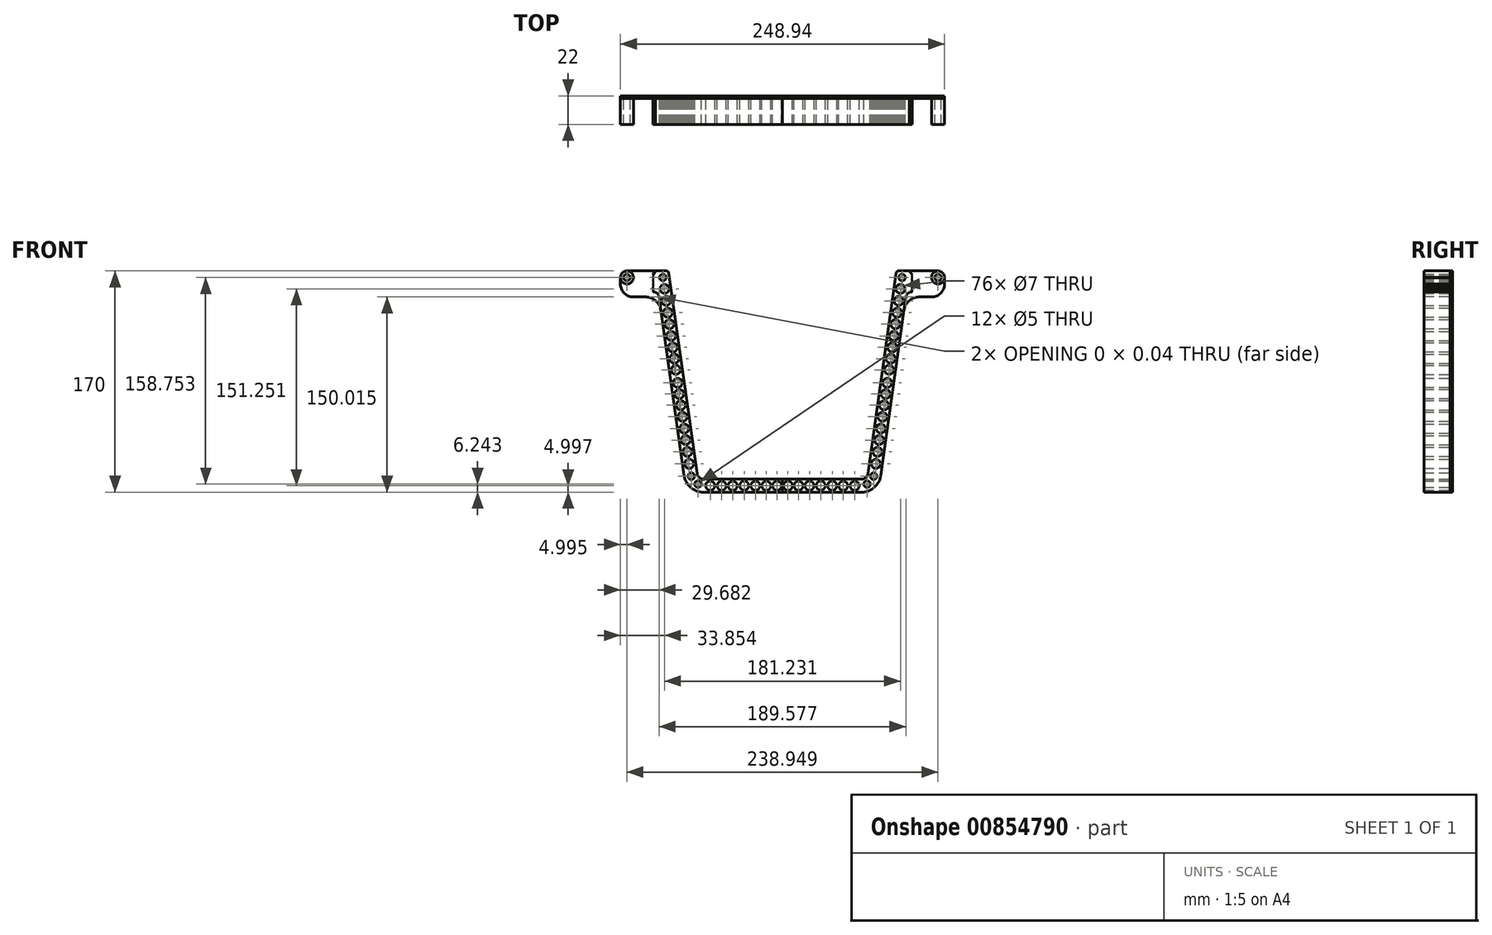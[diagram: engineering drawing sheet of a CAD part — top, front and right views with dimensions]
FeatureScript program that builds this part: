
annotation { "Feature Type Name" : "Feature", "Feature Type Description" : "" }
export const myFeature = defineFeature(function(context is Context, id is Id, definition is map)
    precondition{}
    {
        {
            var Q0;
            Q0=qCreatedBy(makeId("Front.planeOp"),FACE);
            var sketch = newSketch(context, id + "F0", { "sketchPlane" : qUnion([Q0])});
            skLineSegment(sketch, "E0", {"start": v(0, 81.83) * mm, "end": v(0, -78.17) * mm, "construction": true});
            skLineSegment(sketch, "E1", {"start": v(0, -78.17) * mm, "end": v(-65, -78.17) * mm, "construction": true});
            skLineSegment(sketch, "E2", {"start": v(0, 81.83) * mm, "end": v(-87.5, 81.83) * mm, "construction": true});
            skLineSegment(sketch, "E3", {"start": v(-87.5, 81.83) * mm, "end": v(-65, -78.17) * mm, "construction": true});
            skLineSegment(sketch, "E4", {"start": v(-92.55, 81.83) * mm, "end": v(-69.88, -79.36) * mm, "construction": true});
            skLineSegment(sketch, "E5", {"start": v(-87.26, 80.1) * mm, "end": v(-65.6, -73.87) * mm});
            skLineSegment(sketch, "E6", {"start": v(0, -78.17) * mm, "end": v(-60.65, -78.17) * mm});
            skPoint(sketch, "E7.visualSharp", {"position": v(-65, -78.17) * mm});
            skArc(sketch, "E7.filletArc", {"start": v(-65.6, -73.87) * mm, "mid": v(-63.93, -76.95) * mm, "end": v(-60.65, -78.17) * mm});
            skLineSegment(sketch, "E8.0", {"start": v(0, -88.17) * mm, "end": v(-60.65, -88.17) * mm});
            skArc(sketch, "E8.1", {"start": v(-75.5, -75.26) * mm, "mid": v(-70.5, -84.5) * mm, "end": v(-60.65, -88.17) * mm});
            skLineSegment(sketch, "E8.2", {"start": v(-97.4, 80.43) * mm, "end": v(-75.5, -75.26) * mm});
            skLineSegment(sketch, "E9", {"start": v(-89.24, 81.83) * mm, "end": v(-119.47, 81.83) * mm});
            skLineSegment(sketch, "E10", {"start": v(-97.4, 80.43) * mm, "end": v(-97.4, 81.83) * mm});
            skLineSegment(sketch, "E11", {"start": v(-97.4, 81.83) * mm, "end": v(-99.47, 78.83) * mm});
            skLineSegment(sketch, "E12", {"start": v(-119.47, 83.65) * mm, "end": v(-119.47, 55.14) * mm, "construction": true});
            skLineSegment(sketch, "E13", {"start": v(-114.47, 61.83) * mm, "end": v(-94.79, 61.83) * mm});
            skCircle(sketch, "E14", {"center": v(-119.47, 76.83) * mm, "radius": 5 * mm});
            skLineSegment(sketch, "E15", {"start": v(-124.47, 76.98) * mm, "end": v(-124.47, 71.83) * mm});
            skPoint(sketch, "E16.visualSharp", {"position": v(-124.47, 61.83) * mm});
            skArc(sketch, "E16.filletArc", {"start": v(-124.47, 71.83) * mm, "mid": v(-121.54, 64.76) * mm, "end": v(-114.47, 61.83) * mm});
            skCircle(sketch, "E17", {"center": v(-119.47, 76.83) * mm, "radius": 2.5 * mm});
            skArc(sketch, "E18", {"start": v(-93.38, 51.8) * mm, "mid": v(-97.16, 58.9) * mm, "end": v(-104.63, 61.83) * mm});
            skPoint(sketch, "E19.visualSharp", {"position": v(-87.5, 81.83) * mm});
            skArc(sketch, "E19.filletArc", {"start": v(-87.26, 80.1) * mm, "mid": v(-87.93, 81.34) * mm, "end": v(-89.24, 81.83) * mm});
            skLineSegment(sketch, "E20", {"start": v(-119.47, 76.83) * mm, "end": v(-91.85, 76.83) * mm, "construction": true});
            skCircle(sketch, "E21", {"center": v(-91.85, 76.83) * mm, "radius": 2.5 * mm});
            skLineSegment(sketch, "E22.MirrorCS", {"start": v(0, 81.83) * mm, "end": v(87.5, 81.83) * mm, "construction": true});
            skCircle(sketch, "E23", {"center": v(-90.62, 68.08) * mm, "radius": 3.5 * mm});
            skCircle(sketch, "E24", {"center": v(-89.32, 58.86) * mm, "radius": 3.5 * mm});
            skCircle(sketch, "E25", {"center": v(-86.8, 40.96) * mm, "radius": 3.5 * mm});
            skCircle(sketch, "E26", {"center": v(-88.04, 49.78) * mm, "radius": 3.5 * mm});
            skCircle(sketch, "E27", {"center": v(-85.53, 31.92) * mm, "radius": 3.5 * mm});
            skCircle(sketch, "E28", {"center": v(-84.29, 23.08) * mm, "radius": 3.5 * mm});
            skCircle(sketch, "E29", {"center": v(-83.07, 14.45) * mm, "radius": 3.5 * mm});
            skCircle(sketch, "E30", {"center": v(-81.87, 5.86) * mm, "radius": 3.5 * mm});
            skLineSegment(sketch, "E31", {"start": v(-86.11, 0.16) * mm, "end": v(-76.21, 1.55) * mm, "construction": true});
            skCircle(sketch, "E32.MirrorC", {"center": v(-80.46, -4.16) * mm, "radius": 3.5 * mm});
            skCircle(sketch, "E33.MirrorC", {"center": v(-79.25, -12.75) * mm, "radius": 3.5 * mm});
            skCircle(sketch, "E34.MirrorC", {"center": v(-78.04, -21.38) * mm, "radius": 3.5 * mm});
            skCircle(sketch, "E35.MirrorC", {"center": v(-76.8, -30.21) * mm, "radius": 3.5 * mm});
            skCircle(sketch, "E36.MirrorC", {"center": v(-75.52, -39.25) * mm, "radius": 3.5 * mm});
            skCircle(sketch, "E37.MirrorC", {"center": v(-74.28, -48.07) * mm, "radius": 3.5 * mm});
            skCircle(sketch, "E38.MirrorC", {"center": v(-73, -57.15) * mm, "radius": 3.5 * mm});
            skCircle(sketch, "E39.MirrorC", {"center": v(-71.7, -66.37) * mm, "radius": 3.5 * mm});
            skLineSegment(sketch, "E40", {"start": v(0, -83.17) * mm, "end": v(-64.61, -83.17) * mm, "construction": true});
            skCircle(sketch, "E41.MirrorC", {"center": v(-4.17, -83.17) * mm, "radius": 3.5 * mm});
            skCircle(sketch, "E42.MirrorC", {"center": v(-12.38, -83.17) * mm, "radius": 3.5 * mm});
            skCircle(sketch, "E43.MirrorC", {"center": v(-20.76, -83.17) * mm, "radius": 3.5 * mm});
            skCircle(sketch, "E44.MirrorC", {"center": v(-29.37, -83.1) * mm, "radius": 3.5 * mm});
            skCircle(sketch, "E45.MirrorC", {"center": v(-38.19, -83.17) * mm, "radius": 3.5 * mm});
            skCircle(sketch, "E46.MirrorC", {"center": v(-46.66, -83.17) * mm, "radius": 3.5 * mm});
            skCircle(sketch, "E47.MirrorC", {"center": v(-55.45, -83.17) * mm, "radius": 3.5 * mm});
            skCircle(sketch, "E48", {"center": v(-64.89, -81.93) * mm, "radius": 2.5 * mm});
            skCircle(sketch, "E49", {"center": v(-70, -75.84) * mm, "radius": 2.5 * mm});
            skArc(sketch, "E50", {"start": v(-94.79, 61.83) * mm, "mid": v(-96.37, 64.7) * mm, "end": v(-99.47, 65.74) * mm});
            skLineSegment(sketch, "E51", {"start": v(-99.47, 78.83) * mm, "end": v(-99.3, 78.7) * mm});
            skLineSegment(sketch, "E52", {"start": v(-99.3, 78.7) * mm, "end": v(-99.47, 78.58) * mm});
            skLineSegment(sketch, "E53", {"start": v(-99.47, 78.58) * mm, "end": v(-99.3, 78.46) * mm});
            skLineSegment(sketch, "E54", {"start": v(-99.3, 78.46) * mm, "end": v(-99.47, 78.34) * mm});
            skLineSegment(sketch, "E55", {"start": v(-99.47, 78.34) * mm, "end": v(-99.3, 78.21) * mm});
            skLineSegment(sketch, "E56", {"start": v(-99.3, 78.21) * mm, "end": v(-99.47, 78.1) * mm});
            skLineSegment(sketch, "E57", {"start": v(-99.47, 78.1) * mm, "end": v(-99.3, 77.97) * mm});
            skLineSegment(sketch, "E58", {"start": v(-99.3, 77.97) * mm, "end": v(-99.47, 77.84) * mm});
            skLineSegment(sketch, "E59", {"start": v(-99.47, 77.84) * mm, "end": v(-99.3, 77.72) * mm});
            skLineSegment(sketch, "E60", {"start": v(-99.3, 77.72) * mm, "end": v(-99.47, 77.6) * mm});
            skLineSegment(sketch, "E61", {"start": v(-99.47, 77.6) * mm, "end": v(-99.3, 77.48) * mm});
            skLineSegment(sketch, "E62", {"start": v(-99.3, 77.48) * mm, "end": v(-99.47, 77.35) * mm});
            skLineSegment(sketch, "E63", {"start": v(-99.47, 77.35) * mm, "end": v(-99.3, 77.23) * mm});
            skLineSegment(sketch, "E64", {"start": v(-99.3, 77.23) * mm, "end": v(-99.47, 77.1) * mm});
            skLineSegment(sketch, "E65", {"start": v(-99.47, 77.1) * mm, "end": v(-99.3, 76.98) * mm});
            skLineSegment(sketch, "E66", {"start": v(-99.3, 76.98) * mm, "end": v(-99.47, 76.86) * mm});
            skLineSegment(sketch, "E67.MirrorCS", {"start": v(-99.3, 76.67) * mm, "end": v(-99.47, 76.8) * mm});
            skLineSegment(sketch, "E68.MirrorCS", {"start": v(-99.47, 76.55) * mm, "end": v(-99.3, 76.67) * mm});
            skLineSegment(sketch, "E69.MirrorCS", {"start": v(-99.3, 76.42) * mm, "end": v(-99.47, 76.55) * mm});
            skLineSegment(sketch, "E70.MirrorCS", {"start": v(-99.3, 76.18) * mm, "end": v(-99.47, 76.3) * mm});
            skLineSegment(sketch, "E71.MirrorCS", {"start": v(-99.47, 76.06) * mm, "end": v(-99.3, 76.18) * mm});
            skLineSegment(sketch, "E72.MirrorCS", {"start": v(-99.3, 75.93) * mm, "end": v(-99.47, 76.06) * mm});
            skLineSegment(sketch, "E73.MirrorCS", {"start": v(-99.47, 75.8) * mm, "end": v(-99.3, 75.93) * mm});
            skLineSegment(sketch, "E74.MirrorCS", {"start": v(-99.3, 75.69) * mm, "end": v(-99.47, 75.8) * mm});
            skLineSegment(sketch, "E75.MirrorCS", {"start": v(-99.47, 75.56) * mm, "end": v(-99.3, 75.69) * mm});
            skLineSegment(sketch, "E76.MirrorCS", {"start": v(-99.3, 75.44) * mm, "end": v(-99.47, 75.56) * mm});
            skLineSegment(sketch, "E77.MirrorCS", {"start": v(-99.47, 75.32) * mm, "end": v(-99.3, 75.44) * mm});
            skLineSegment(sketch, "E78.MirrorCS", {"start": v(-99.3, 75.2) * mm, "end": v(-99.47, 75.32) * mm});
            skLineSegment(sketch, "E79.MirrorCS", {"start": v(-99.47, 75.07) * mm, "end": v(-99.3, 75.2) * mm});
            skLineSegment(sketch, "E80.MirrorCS", {"start": v(-99.3, 74.95) * mm, "end": v(-99.47, 75.07) * mm});
            skLineSegment(sketch, "E81.MirrorCS", {"start": v(-99.47, 74.83) * mm, "end": v(-99.3, 74.95) * mm});
            skLineSegment(sketch, "E82.MirrorCS", {"start": v(-99.47, 76.3) * mm, "end": v(-99.3, 76.42) * mm});
            skLineSegment(sketch, "E83", {"start": v(-99.47, 74.83) * mm, "end": v(-99.3, 74.7) * mm});
            skLineSegment(sketch, "E84", {"start": v(-99.3, 74.7) * mm, "end": v(-99.47, 74.58) * mm});
            skLineSegment(sketch, "E85", {"start": v(-99.47, 74.58) * mm, "end": v(-99.3, 74.46) * mm});
            skLineSegment(sketch, "E86", {"start": v(-99.3, 74.46) * mm, "end": v(-99.47, 74.33) * mm});
            skLineSegment(sketch, "E87", {"start": v(-99.47, 74.33) * mm, "end": v(-99.3, 74.2) * mm});
            skLineSegment(sketch, "E88", {"start": v(-99.3, 74.2) * mm, "end": v(-99.47, 74.09) * mm});
            skLineSegment(sketch, "E89", {"start": v(-99.47, 74.09) * mm, "end": v(-99.3, 73.96) * mm});
            skLineSegment(sketch, "E90", {"start": v(-99.3, 73.96) * mm, "end": v(-99.47, 73.84) * mm});
            skLineSegment(sketch, "E91", {"start": v(-99.47, 73.84) * mm, "end": v(-99.3, 73.72) * mm});
            skLineSegment(sketch, "E92", {"start": v(-99.3, 73.72) * mm, "end": v(-99.47, 73.6) * mm});
            skLineSegment(sketch, "E93", {"start": v(-99.47, 73.6) * mm, "end": v(-99.3, 73.47) * mm});
            skLineSegment(sketch, "E94", {"start": v(-99.3, 73.47) * mm, "end": v(-99.47, 73.35) * mm});
            skLineSegment(sketch, "E95", {"start": v(-99.47, 73.35) * mm, "end": v(-99.3, 73.23) * mm});
            skLineSegment(sketch, "E96", {"start": v(-99.3, 73.23) * mm, "end": v(-99.47, 73.1) * mm});
            skLineSegment(sketch, "E97", {"start": v(-99.47, 73.1) * mm, "end": v(-99.3, 72.98) * mm});
            skLineSegment(sketch, "E98", {"start": v(-99.3, 72.98) * mm, "end": v(-99.47, 72.86) * mm});
            skLineSegment(sketch, "E99.MirrorCS", {"start": v(-99.3, 72.67) * mm, "end": v(-99.47, 72.8) * mm});
            skLineSegment(sketch, "E100.MirrorCS", {"start": v(-99.47, 72.54) * mm, "end": v(-99.3, 72.67) * mm});
            skLineSegment(sketch, "E101.MirrorCS", {"start": v(-99.47, 72.05) * mm, "end": v(-99.3, 72.17) * mm});
            skLineSegment(sketch, "E102.MirrorCS", {"start": v(-99.3, 71.93) * mm, "end": v(-99.47, 72.05) * mm});
            skLineSegment(sketch, "E103.MirrorCS", {"start": v(-99.47, 71.8) * mm, "end": v(-99.3, 71.93) * mm});
            skLineSegment(sketch, "E104.MirrorCS", {"start": v(-99.3, 71.68) * mm, "end": v(-99.47, 71.8) * mm});
            skLineSegment(sketch, "E105.MirrorCS", {"start": v(-99.47, 71.56) * mm, "end": v(-99.3, 71.68) * mm});
            skLineSegment(sketch, "E106.MirrorCS", {"start": v(-99.3, 71.44) * mm, "end": v(-99.47, 71.56) * mm});
            skLineSegment(sketch, "E107.MirrorCS", {"start": v(-99.47, 71.31) * mm, "end": v(-99.3, 71.44) * mm});
            skLineSegment(sketch, "E108.MirrorCS", {"start": v(-99.3, 71.2) * mm, "end": v(-99.47, 71.31) * mm});
            skLineSegment(sketch, "E109.MirrorCS", {"start": v(-99.47, 71.07) * mm, "end": v(-99.3, 71.2) * mm});
            skLineSegment(sketch, "E110.MirrorCS", {"start": v(-99.3, 70.94) * mm, "end": v(-99.47, 71.07) * mm});
            skLineSegment(sketch, "E111.MirrorCS", {"start": v(-99.47, 70.82) * mm, "end": v(-99.3, 70.94) * mm});
            skLineSegment(sketch, "E112.MirrorCS", {"start": v(-99.3, 72.42) * mm, "end": v(-99.47, 72.54) * mm});
            skLineSegment(sketch, "E113.MirrorCS", {"start": v(-99.3, 72.17) * mm, "end": v(-99.47, 72.3) * mm});
            skLineSegment(sketch, "E114.MirrorCS", {"start": v(-99.47, 72.3) * mm, "end": v(-99.3, 72.42) * mm});
            skLineSegment(sketch, "E115", {"start": v(-99.47, 70.82) * mm, "end": v(-99.3, 70.7) * mm});
            skLineSegment(sketch, "E116", {"start": v(-99.3, 70.7) * mm, "end": v(-99.47, 70.58) * mm});
            skLineSegment(sketch, "E117", {"start": v(-99.47, 70.58) * mm, "end": v(-99.3, 70.45) * mm});
            skLineSegment(sketch, "E118", {"start": v(-99.3, 70.45) * mm, "end": v(-99.47, 70.33) * mm});
            skLineSegment(sketch, "E119", {"start": v(-99.47, 70.33) * mm, "end": v(-99.3, 70.2) * mm});
            skLineSegment(sketch, "E120", {"start": v(-99.3, 70.2) * mm, "end": v(-99.47, 70.08) * mm});
            skLineSegment(sketch, "E121", {"start": v(-99.47, 70.08) * mm, "end": v(-99.3, 69.96) * mm});
            skLineSegment(sketch, "E122", {"start": v(-99.3, 69.96) * mm, "end": v(-99.47, 69.84) * mm});
            skLineSegment(sketch, "E123", {"start": v(-99.47, 69.84) * mm, "end": v(-99.3, 69.71) * mm});
            skLineSegment(sketch, "E124", {"start": v(-99.3, 69.71) * mm, "end": v(-99.47, 69.6) * mm});
            skLineSegment(sketch, "E125", {"start": v(-99.47, 69.6) * mm, "end": v(-99.3, 69.47) * mm});
            skLineSegment(sketch, "E126", {"start": v(-99.3, 69.47) * mm, "end": v(-99.47, 69.34) * mm});
            skLineSegment(sketch, "E127", {"start": v(-99.47, 69.34) * mm, "end": v(-99.3, 69.22) * mm});
            skLineSegment(sketch, "E128", {"start": v(-99.3, 69.22) * mm, "end": v(-99.47, 69.1) * mm});
            skLineSegment(sketch, "E129", {"start": v(-99.47, 69.1) * mm, "end": v(-99.3, 68.98) * mm});
            skLineSegment(sketch, "E130", {"start": v(-99.3, 68.98) * mm, "end": v(-99.47, 68.85) * mm});
            skLineSegment(sketch, "E131.MirrorCS", {"start": v(-99.3, 68.66) * mm, "end": v(-99.47, 68.79) * mm});
            skLineSegment(sketch, "E132.MirrorCS", {"start": v(-99.47, 68.54) * mm, "end": v(-99.3, 68.66) * mm});
            skLineSegment(sketch, "E133.MirrorCS", {"start": v(-99.47, 68.05) * mm, "end": v(-99.3, 68.17) * mm});
            skLineSegment(sketch, "E134.MirrorCS", {"start": v(-99.3, 67.93) * mm, "end": v(-99.47, 68.05) * mm});
            skLineSegment(sketch, "E135.MirrorCS", {"start": v(-99.47, 67.8) * mm, "end": v(-99.3, 67.93) * mm});
            skLineSegment(sketch, "E136.MirrorCS", {"start": v(-99.3, 67.68) * mm, "end": v(-99.47, 67.8) * mm});
            skLineSegment(sketch, "E137.MirrorCS", {"start": v(-99.47, 67.56) * mm, "end": v(-99.3, 67.68) * mm});
            skLineSegment(sketch, "E138.MirrorCS", {"start": v(-99.3, 67.43) * mm, "end": v(-99.47, 67.56) * mm});
            skLineSegment(sketch, "E139.MirrorCS", {"start": v(-99.47, 67.3) * mm, "end": v(-99.3, 67.43) * mm});
            skLineSegment(sketch, "E140.MirrorCS", {"start": v(-99.3, 67.19) * mm, "end": v(-99.47, 67.3) * mm});
            skLineSegment(sketch, "E141.MirrorCS", {"start": v(-99.47, 67.06) * mm, "end": v(-99.3, 67.19) * mm});
            skLineSegment(sketch, "E142.MirrorCS", {"start": v(-99.3, 66.94) * mm, "end": v(-99.47, 67.06) * mm});
            skLineSegment(sketch, "E143.MirrorCS", {"start": v(-99.47, 66.82) * mm, "end": v(-99.3, 66.94) * mm});
            skLineSegment(sketch, "E144.MirrorCS", {"start": v(-99.3, 68.42) * mm, "end": v(-99.47, 68.54) * mm});
            skLineSegment(sketch, "E145.MirrorCS", {"start": v(-99.3, 68.17) * mm, "end": v(-99.47, 68.3) * mm});
            skLineSegment(sketch, "E146.MirrorCS", {"start": v(-99.47, 68.3) * mm, "end": v(-99.3, 68.42) * mm});
            skLineSegment(sketch, "E147.MirrorCS", {"start": v(-99.3, 66.7) * mm, "end": v(-99.47, 66.82) * mm});
            skLineSegment(sketch, "E148.MirrorCS", {"start": v(-99.47, 66.57) * mm, "end": v(-99.3, 66.7) * mm});
            skLineSegment(sketch, "E149.MirrorCS", {"start": v(-99.3, 66.45) * mm, "end": v(-99.47, 66.57) * mm});
            skLineSegment(sketch, "E150.MirrorCS", {"start": v(-99.47, 66.33) * mm, "end": v(-99.3, 66.45) * mm});
            skLineSegment(sketch, "E151.MirrorCS", {"start": v(-99.3, 66.2) * mm, "end": v(-99.47, 66.33) * mm});
            skLineSegment(sketch, "E152.MirrorCS", {"start": v(-99.47, 66.08) * mm, "end": v(-99.3, 66.2) * mm});
            skLineSegment(sketch, "E153.MirrorCS", {"start": v(-99.3, 65.96) * mm, "end": v(-99.47, 66.08) * mm});
            skLineSegment(sketch, "E154.MirrorCS", {"start": v(-99.47, 65.83) * mm, "end": v(-99.3, 65.96) * mm});
            skLineSegment(sketch, "E155", {"start": v(-99.47, 65.83) * mm, "end": v(-99.47, 65.74) * mm});
            skLineSegment(sketch, "E156", {"start": v(-99.47, 76.86) * mm, "end": v(-99.47, 76.8) * mm});
            skLineSegment(sketch, "E157", {"start": v(-99.47, 72.8) * mm, "end": v(-99.47, 72.86) * mm});
            skLineSegment(sketch, "E158", {"start": v(-99.47, 68.79) * mm, "end": v(-99.47, 68.85) * mm});
            skLineSegment(sketch, "E159.MirrorCS", {"start": v(0, -83.17) * mm, "end": v(64.61, -83.17) * mm, "construction": true});
            skLineSegment(sketch, "E160", {"start": v(0, -78.17) * mm, "end": v(0, -88.17) * mm});
            skSolve(sketch);
        }
        {
            var Q0;
            {var subQ0=sQuery(id+"F0.wireOp",EDGE,"E15");var subQ1=sQuery(id+"F0.wireOp",EDGE,"E14");var subQ2=makeQuery(id+"F0.imprint","INTERSECT",VERTEX,{"disambiguationData":[OD(0.0)],"derivedFrom":[subQ1,subQ0]});Q0=makeQuery(id+"F0.imprint","IMPRINT",FACE,{"disambiguationData":[TD([[makeQuery(id+"F0.imprint","IMPRINT",EDGE,{"disambiguationData":[TD([[subQ2,-1.0]])],"derivedFrom":subQ1}),1.0]])]});}
            var Q1;
            {var subQ0=sQuery(id+"F0.wireOp",EDGE,"0dbe8d11-749e-4dd8-bf5f-606088edf9f938.MirrorC");var subQ1=sQuery(id+"F0.wireOp",EDGE,"0dbe8d11-749e-4dd8-bf5f-606088edf9f913.MirrorCS");var subQ2=makeQuery(id+"F0.imprint","INTERSECT",VERTEX,{"disambiguationData":[OD(0.0)],"derivedFrom":[subQ1,subQ0]});Q1=makeQuery(id+"F0.imprint","IMPRINT",FACE,{"disambiguationData":[TD([[makeQuery(id+"F0.imprint","IMPRINT",EDGE,{"disambiguationData":[TD([[subQ2,-1.0]])],"derivedFrom":subQ1}),1.0]])]});}
            var Q2;
            Q2=makeQuery(id+"F0.imprint","IMPRINT",FACE,{"disambiguationData":[TD([[makeQuery(id+"F0.imprint","IMPRINT",EDGE,{"derivedFrom":sQuery(id+"F0.wireOp",EDGE,"0dbe8d11-749e-4dd8-bf5f-606088edf9f90.MirrorCS")}),-1.0]])]});
            var Q3;
            Q3=makeQuery(id+"F0.imprint","IMPRINT",FACE,{"disambiguationData":[TD([[makeQuery(id+"F0.imprint","IMPRINT",EDGE,{"derivedFrom":sQuery(id+"F0.wireOp",EDGE,"E17")}),-1.0]])]});
            var Q4;
            Q4=makeQuery(id+"F0.imprint","IMPRINT",FACE,{"disambiguationData":[TD([[makeQuery(id+"F0.imprint","IMPRINT",EDGE,{"derivedFrom":sQuery(id+"F0.wireOp",EDGE,"0dDpVTIy-GunA-bBvD-cwDT-sV3W6Ews1qMp")}),-1.0]])]});
            var Q5;
            Q5=makeQuery(id+"F0.imprint","IMPRINT",FACE,{"disambiguationData":[TD([[makeQuery(id+"F0.imprint","IMPRINT",EDGE,{"derivedFrom":sQuery(id+"F0.wireOp",EDGE,"0dbe8d11-749e-4dd8-bf5f-606088edf9f915.MirrorC")}),1.0]])]});
            var Q6;
            Q6=makeQuery(id+"F0.imprint","IMPRINT",FACE,{"disambiguationData":[TD([[makeQuery(id+"F0.imprint","IMPRINT",EDGE,{"derivedFrom":sQuery(id+"F0.wireOp",EDGE,"0dbe8d11-749e-4dd8-bf5f-606088edf9f927.MirrorC")}),1.0]])]});
            var Q7;
            Q7=makeQuery(id+"F0.imprint","IMPRINT",FACE,{"disambiguationData":[TD([[makeQuery(id+"F0.imprint","IMPRINT",EDGE,{"derivedFrom":sQuery(id+"F0.wireOp",EDGE,"E5")}),-1.0]])]});
            var Q8;
            {var subQ6=sQuery(id+"F0.wireOp",EDGE,"E10");Q8=makeQuery(id+"F0.imprint","IMPRINT",FACE,{"disambiguationData":[TD([[makeQuery(id+"F0.imprint","IMPRINT",EDGE,{"derivedFrom":subQ6}),1.0]])]});}
            var Q9;
            Q9=makeQuery(id+"F0.imprint","IMPRINT",FACE,{"disambiguationData":[TD([[makeQuery(id+"F0.imprint","IMPRINT",EDGE,{"derivedFrom":sQuery(id+"F0.wireOp",EDGE,"146d1f34-d285-41d7-8e35-71dadb03bad80.MirrorCS")}),1.0]])]});
            var Q10;
            Q10=makeQuery(id+"F0.imprint","IMPRINT",FACE,{"disambiguationData":[TD([[makeQuery(id+"F0.imprint","IMPRINT",EDGE,{"derivedFrom":sQuery(id+"F0.wireOp",EDGE,"edc6cb30-b65f-47d9-9bdc-20ee79fae63b0.MirrorCS")}),1.0]])]});
            var Q11;
            Q11=makeQuery(id+"F0.imprint","IMPRINT",FACE,{"disambiguationData":[TD([[makeQuery(id+"F0.imprint","IMPRINT",EDGE,{"derivedFrom":sQuery(id+"F0.wireOp",EDGE,"edc6cb30-b65f-47d9-9bdc-20ee79fae63b120.MirrorC")}),1.0]])]});
            var Q12;
            Q12=makeQuery(id+"F0.imprint","IMPRINT",FACE,{"disambiguationData":[TD([[makeQuery(id+"F0.imprint","IMPRINT",EDGE,{"derivedFrom":sQuery(id+"F0.wireOp",EDGE,"4b3109ea-8a59-4b7b-b5cc-42d9bb3fa2250.MirrorC")}),1.0]])]});
            extrude(context, id + "F1", {"entities" : qUnion([Q0, Q1, Q2, Q3, Q4, Q5, Q6, Q7, Q8, Q9, Q10, Q11, Q12]), "depth" : 20 * mm, "offsetDistance" : 25 * mm});
        }
        {
            var Q0;
            {var subQ0=sQuery(id+"F0.wireOp",EDGE,"E15");var subQ1=sQuery(id+"F0.wireOp",EDGE,"E14");var subQ2=makeQuery(id+"F0.imprint","INTERSECT",VERTEX,{"disambiguationData":[OD(0.0)],"derivedFrom":[subQ1,subQ0]});Q0=makeQuery(id+"F0.imprint","IMPRINT",FACE,{"disambiguationData":[TD([[makeQuery(id+"F0.imprint","IMPRINT",EDGE,{"disambiguationData":[TD([[subQ2,-1.0]])],"derivedFrom":subQ1}),1.0]])]});}
            var Q1;
            {var subQ0=sQuery(id+"F0.wireOp",EDGE,"0dbe8d11-749e-4dd8-bf5f-606088edf9f938.MirrorC");var subQ1=sQuery(id+"F0.wireOp",EDGE,"0dbe8d11-749e-4dd8-bf5f-606088edf9f913.MirrorCS");var subQ2=makeQuery(id+"F0.imprint","INTERSECT",VERTEX,{"disambiguationData":[OD(0.0)],"derivedFrom":[subQ1,subQ0]});Q1=makeQuery(id+"F0.imprint","IMPRINT",FACE,{"disambiguationData":[TD([[makeQuery(id+"F0.imprint","IMPRINT",EDGE,{"disambiguationData":[TD([[subQ2,-1.0]])],"derivedFrom":subQ1}),1.0]])]});}
            var Q2;
            {var subQ0=sQuery(id+"F0.wireOp",EDGE,"E10");Q2=makeQuery(id+"F0.imprint","IMPRINT",FACE,{"disambiguationData":[TD([[makeQuery(id+"F0.imprint","IMPRINT",EDGE,{"derivedFrom":subQ0}),1.0]])]});}
            var Q3;
            {var subQ0=sQuery(id+"F0.wireOp",EDGE,"E13");var subQ1=sQuery(id+"F0.wireOp",EDGE,"E8.2");var subQ2=makeQuery(id+"F0.imprint","INTERSECT",VERTEX,{"derivedFrom":[subQ1,subQ0]});Q3=makeQuery(id+"F0.imprint","IMPRINT",FACE,{"disambiguationData":[TD([[makeQuery(id+"F0.imprint","IMPRINT",EDGE,{"disambiguationData":[TD([[subQ2,-1.0]])],"derivedFrom":subQ1}),-1.0]])]});}
            var Q4;
            Q4=makeQuery(id+"F0.imprint","IMPRINT",FACE,{"disambiguationData":[TD([[makeQuery(id+"F0.imprint","IMPRINT",EDGE,{"derivedFrom":sQuery(id+"F0.wireOp",EDGE,"0dbe8d11-749e-4dd8-bf5f-606088edf9f90.MirrorCS")}),-1.0]])]});
            var Q5;
            {var subQ0=sQuery(id+"F0.wireOp",EDGE,"0dbe8d11-749e-4dd8-bf5f-606088edf9f917.MirrorCS");Q5=makeQuery(id+"F0.imprint","IMPRINT",FACE,{"disambiguationData":[TD([[makeQuery(id+"F0.imprint","IMPRINT",EDGE,{"derivedFrom":subQ0}),1.0]])]});}
            var Q6;
            Q6=makeQuery(id+"F0.imprint","IMPRINT",FACE,{"disambiguationData":[TD([[makeQuery(id+"F0.imprint","IMPRINT",EDGE,{"derivedFrom":sQuery(id+"F0.wireOp",EDGE,"E17")}),-1.0]])]});
            var Q7;
            Q7=makeQuery(id+"F0.imprint","IMPRINT",FACE,{"disambiguationData":[TD([[makeQuery(id+"F0.imprint","IMPRINT",EDGE,{"derivedFrom":sQuery(id+"F0.wireOp",EDGE,"0dbe8d11-749e-4dd8-bf5f-606088edf9f915.MirrorC")}),1.0]])]});
            var Q8;
            Q8=makeQuery(id+"F0.imprint","IMPRINT",FACE,{"disambiguationData":[TD([[makeQuery(id+"F0.imprint","IMPRINT",EDGE,{"derivedFrom":sQuery(id+"F0.wireOp",EDGE,"0dbe8d11-749e-4dd8-bf5f-606088edf9f90.MirrorCS")}),1.0]])]});
            var Q9;
            Q9=makeQuery(id+"F0.imprint","IMPRINT",FACE,{"disambiguationData":[TD([[makeQuery(id+"F0.imprint","IMPRINT",EDGE,{"derivedFrom":sQuery(id+"F0.wireOp",EDGE,"E5")}),-1.0]])]});
            var Q10;
            Q10=makeQuery(id+"F1.opExtrude","CAP_FACE",FACE,{"disambiguationData":[OSD([sQuery(id+"F0.wireOp",EDGE,"0dbe8d11-749e-4dd8-bf5f-606088edf9f927.MirrorC"),sQuery(id+"F0.wireOp",EDGE,"0dbe8d11-749e-4dd8-bf5f-606088edf9f930.MirrorC"),sQuery(id+"F0.wireOp",EDGE,"0dbe8d11-749e-4dd8-bf5f-606088edf9f937.MirrorC"),sQuery(id+"F0.wireOp",EDGE,"0dbe8d11-749e-4dd8-bf5f-606088edf9f939.MirrorC")])],"isStart":true});
            var Q11;
            Q11=makeQuery(id+"F1.opExtrude","CAP_FACE",FACE,{"disambiguationData":[OSD([sQuery(id+"F0.wireOp",EDGE,"0dDpVTIy-GunA-bBvD-cwDT-sV3W6Ews1qMp"),sQuery(id+"F0.wireOp",EDGE,"DaxXs096-5P6e-ln3i-1fls-EDtKtiFNkicc"),sQuery(id+"F0.wireOp",EDGE,"9CA4RQp1-Vh6f-FTdw-iHL7-ZiKy4ZHbnpA4"),sQuery(id+"F0.wireOp",EDGE,"8MmCyf6s-D1jL-yhrz-7HK1-GQKixaBdKuq5")])],"isStart":true});
            var Q12;
            Q12=makeQuery(id+"F0.imprint","IMPRINT",FACE,{"disambiguationData":[TD([[makeQuery(id+"F0.imprint","IMPRINT",EDGE,{"derivedFrom":sQuery(id+"F0.wireOp",EDGE,"6fafdf1c-5a9f-42b9-8fca-69171c2090fe0.MirrorC")}),-1.0]])]});
            var Q13;
            Q13=makeQuery(id+"F0.imprint","IMPRINT",FACE,{"disambiguationData":[TD([[makeQuery(id+"F0.imprint","IMPRINT",EDGE,{"derivedFrom":sQuery(id+"F0.wireOp",EDGE,"5d7c4930-5d35-44d2-abbe-bf8a046e604b0.MirrorC")}),-1.0]])]});
            var Q14;
            Q14=makeQuery(id+"F0.imprint","IMPRINT",FACE,{"disambiguationData":[TD([[makeQuery(id+"F0.imprint","IMPRINT",EDGE,{"derivedFrom":sQuery(id+"F0.wireOp",EDGE,"93e47cc0-b65f-49ba-a826-1170111759de0.MirrorC")}),-1.0]])]});
            var Q15;
            Q15=makeQuery(id+"F0.imprint","IMPRINT",FACE,{"disambiguationData":[TD([[makeQuery(id+"F0.imprint","IMPRINT",EDGE,{"derivedFrom":sQuery(id+"F0.wireOp",EDGE,"31a9611e-6eb8-4856-a295-34dcad6ab40d0.MirrorC")}),-1.0]])]});
            var Q16;
            Q16=makeQuery(id+"F0.imprint","IMPRINT",FACE,{"disambiguationData":[TD([[makeQuery(id+"F0.imprint","IMPRINT",EDGE,{"derivedFrom":sQuery(id+"F0.wireOp",EDGE,"c8a62252-939b-45ef-ba5b-4b47af7ec5bc0.MirrorC")}),-1.0]])]});
            var Q17;
            Q17=makeQuery(id+"F0.imprint","IMPRINT",FACE,{"disambiguationData":[TD([[makeQuery(id+"F0.imprint","IMPRINT",EDGE,{"derivedFrom":sQuery(id+"F0.wireOp",EDGE,"4e314b3c-e5cf-44cd-9bb4-30ff3c9f04900.MirrorC")}),-1.0]])]});
            var Q18;
            Q18=makeQuery(id+"F0.imprint","IMPRINT",FACE,{"disambiguationData":[TD([[makeQuery(id+"F0.imprint","IMPRINT",EDGE,{"derivedFrom":sQuery(id+"F0.wireOp",EDGE,"0e234889-f3b6-42e5-a6bf-3698e1ddfbc70.MirrorC")}),-1.0]])]});
            var Q19;
            Q19=makeQuery(id+"F0.imprint","IMPRINT",FACE,{"disambiguationData":[TD([[makeQuery(id+"F0.imprint","IMPRINT",EDGE,{"derivedFrom":sQuery(id+"F0.wireOp",EDGE,"b8a3a664-10cd-4da3-87f1-6c564825d5060.MirrorC")}),-1.0]])]});
            var Q20;
            Q20=makeQuery(id+"F0.imprint","IMPRINT",FACE,{"disambiguationData":[TD([[makeQuery(id+"F0.imprint","IMPRINT",EDGE,{"derivedFrom":sQuery(id+"F0.wireOp",EDGE,"7c9d9746-946a-4a82-93a4-e8250d0407200.MirrorC")}),1.0]])]});
            var Q21;
            Q21=makeQuery(id+"F0.imprint","IMPRINT",FACE,{"disambiguationData":[TD([[makeQuery(id+"F0.imprint","IMPRINT",EDGE,{"derivedFrom":sQuery(id+"F0.wireOp",EDGE,"9c584d2b-6716-421a-94f2-c0d29ae9cc4a0.MirrorC")}),1.0]])]});
            var Q22;
            Q22=makeQuery(id+"F0.imprint","IMPRINT",FACE,{"disambiguationData":[TD([[makeQuery(id+"F0.imprint","IMPRINT",EDGE,{"derivedFrom":sQuery(id+"F0.wireOp",EDGE,"e290275b-f84c-4f5e-a9ad-dbf2d7fec2ba0.MirrorC")}),1.0]])]});
            var Q23;
            Q23=makeQuery(id+"F0.imprint","IMPRINT",FACE,{"disambiguationData":[TD([[makeQuery(id+"F0.imprint","IMPRINT",EDGE,{"derivedFrom":sQuery(id+"F0.wireOp",EDGE,"f6b15b81-bd99-4128-83e3-99ece5be16820.MirrorC")}),1.0]])]});
            var Q24;
            Q24=makeQuery(id+"F0.imprint","IMPRINT",FACE,{"disambiguationData":[TD([[makeQuery(id+"F0.imprint","IMPRINT",EDGE,{"derivedFrom":sQuery(id+"F0.wireOp",EDGE,"fdfc75b4-a94d-4347-972d-14ef7b3f4e7c0.MirrorC")}),1.0]])]});
            var Q25;
            Q25=makeQuery(id+"F0.imprint","IMPRINT",FACE,{"disambiguationData":[TD([[makeQuery(id+"F0.imprint","IMPRINT",EDGE,{"derivedFrom":sQuery(id+"F0.wireOp",EDGE,"ccf916eb-6706-4f8d-a0d9-161ba939b9130.MirrorC")}),1.0]])]});
            var Q26;
            Q26=makeQuery(id+"F0.imprint","IMPRINT",FACE,{"disambiguationData":[TD([[makeQuery(id+"F0.imprint","IMPRINT",EDGE,{"derivedFrom":sQuery(id+"F0.wireOp",EDGE,"06e9775e-e3b1-4474-a2ca-ba4f2cbe0e660.MirrorC")}),1.0]])]});
            var Q27;
            Q27=makeQuery(id+"F0.imprint","IMPRINT",FACE,{"disambiguationData":[TD([[makeQuery(id+"F0.imprint","IMPRINT",EDGE,{"derivedFrom":sQuery(id+"F0.wireOp",EDGE,"305a2a2c-549e-41e6-b30a-6479f73e64ae0.MirrorC")}),1.0]])]});
            var Q28;
            Q28=makeQuery(id+"F0.imprint","IMPRINT",FACE,{"disambiguationData":[TD([[makeQuery(id+"F0.imprint","IMPRINT",EDGE,{"derivedFrom":sQuery(id+"F0.wireOp",EDGE,"0211aa2d-060f-4f7e-aa11-442e97ad2fa90.MirrorC")}),-1.0]])]});
            var Q29;
            Q29=makeQuery(id+"F0.imprint","IMPRINT",FACE,{"disambiguationData":[TD([[makeQuery(id+"F0.imprint","IMPRINT",EDGE,{"derivedFrom":sQuery(id+"F0.wireOp",EDGE,"118c0752-2b39-4778-ae3b-7c2d176b19220.MirrorC")}),1.0]])]});
            var Q30;
            Q30=makeQuery(id+"F0.imprint","IMPRINT",FACE,{"disambiguationData":[TD([[makeQuery(id+"F0.imprint","IMPRINT",EDGE,{"derivedFrom":sQuery(id+"F0.wireOp",EDGE,"4c30d257-ae61-41e1-884f-7782ecb3eac70.MirrorC")}),1.0]])]});
            var Q31;
            Q31=makeQuery(id+"F0.imprint","IMPRINT",FACE,{"disambiguationData":[TD([[makeQuery(id+"F0.imprint","IMPRINT",EDGE,{"derivedFrom":sQuery(id+"F0.wireOp",EDGE,"de977714-783d-4bda-950a-1716b40ce7890.MirrorC")}),1.0]])]});
            var Q32;
            Q32=makeQuery(id+"F0.imprint","IMPRINT",FACE,{"disambiguationData":[TD([[makeQuery(id+"F0.imprint","IMPRINT",EDGE,{"derivedFrom":sQuery(id+"F0.wireOp",EDGE,"ef58f09d-46bd-4b9f-97cd-23ce397a92870.MirrorC")}),1.0]])]});
            var Q33;
            Q33=makeQuery(id+"F0.imprint","IMPRINT",FACE,{"disambiguationData":[TD([[makeQuery(id+"F0.imprint","IMPRINT",EDGE,{"derivedFrom":sQuery(id+"F0.wireOp",EDGE,"37420363-67b0-4566-8541-87a9eb782f470.MirrorC")}),1.0]])]});
            var Q34;
            Q34=makeQuery(id+"F0.imprint","IMPRINT",FACE,{"disambiguationData":[TD([[makeQuery(id+"F0.imprint","IMPRINT",EDGE,{"derivedFrom":sQuery(id+"F0.wireOp",EDGE,"0fa02fb8-987e-41aa-9684-bbdc1dcf14ef0.MirrorC")}),1.0]])]});
            var Q35;
            Q35=makeQuery(id+"F0.imprint","IMPRINT",FACE,{"disambiguationData":[TD([[makeQuery(id+"F0.imprint","IMPRINT",EDGE,{"derivedFrom":sQuery(id+"F0.wireOp",EDGE,"eef8f519-72dc-489c-bfe9-dd3af72a4c800.MirrorC")}),1.0]])]});
            var Q36;
            Q36=makeQuery(id+"F0.imprint","IMPRINT",FACE,{"disambiguationData":[TD([[makeQuery(id+"F0.imprint","IMPRINT",EDGE,{"derivedFrom":sQuery(id+"F0.wireOp",EDGE,"E41.MirrorC")}),-1.0]])]});
            var Q37;
            Q37=makeQuery(id+"F0.imprint","IMPRINT",FACE,{"disambiguationData":[TD([[makeQuery(id+"F0.imprint","IMPRINT",EDGE,{"derivedFrom":sQuery(id+"F0.wireOp",EDGE,"E42.MirrorC")}),-1.0]])]});
            var Q38;
            Q38=makeQuery(id+"F0.imprint","IMPRINT",FACE,{"disambiguationData":[TD([[makeQuery(id+"F0.imprint","IMPRINT",EDGE,{"derivedFrom":sQuery(id+"F0.wireOp",EDGE,"E43.MirrorC")}),-1.0]])]});
            var Q39;
            Q39=makeQuery(id+"F0.imprint","IMPRINT",FACE,{"disambiguationData":[TD([[makeQuery(id+"F0.imprint","IMPRINT",EDGE,{"derivedFrom":sQuery(id+"F0.wireOp",EDGE,"E44.MirrorC")}),-1.0]])]});
            var Q40;
            Q40=makeQuery(id+"F0.imprint","IMPRINT",FACE,{"disambiguationData":[TD([[makeQuery(id+"F0.imprint","IMPRINT",EDGE,{"derivedFrom":sQuery(id+"F0.wireOp",EDGE,"E45.MirrorC")}),-1.0]])]});
            var Q41;
            Q41=makeQuery(id+"F0.imprint","IMPRINT",FACE,{"disambiguationData":[TD([[makeQuery(id+"F0.imprint","IMPRINT",EDGE,{"derivedFrom":sQuery(id+"F0.wireOp",EDGE,"E46.MirrorC")}),-1.0]])]});
            var Q42;
            Q42=makeQuery(id+"F0.imprint","IMPRINT",FACE,{"disambiguationData":[TD([[makeQuery(id+"F0.imprint","IMPRINT",EDGE,{"derivedFrom":sQuery(id+"F0.wireOp",EDGE,"E47.MirrorC")}),-1.0]])]});
            var Q43;
            Q43=makeQuery(id+"F0.imprint","IMPRINT",FACE,{"disambiguationData":[TD([[makeQuery(id+"F0.imprint","IMPRINT",EDGE,{"derivedFrom":sQuery(id+"F0.wireOp",EDGE,"E48")}),1.0]])]});
            var Q44;
            Q44=makeQuery(id+"F0.imprint","IMPRINT",FACE,{"disambiguationData":[TD([[makeQuery(id+"F0.imprint","IMPRINT",EDGE,{"derivedFrom":sQuery(id+"F0.wireOp",EDGE,"E49")}),1.0]])]});
            var Q45;
            Q45=makeQuery(id+"F0.imprint","IMPRINT",FACE,{"disambiguationData":[TD([[makeQuery(id+"F0.imprint","IMPRINT",EDGE,{"derivedFrom":sQuery(id+"F0.wireOp",EDGE,"E39.MirrorC")}),-1.0]])]});
            var Q46;
            Q46=makeQuery(id+"F0.imprint","IMPRINT",FACE,{"disambiguationData":[TD([[makeQuery(id+"F0.imprint","IMPRINT",EDGE,{"derivedFrom":sQuery(id+"F0.wireOp",EDGE,"E38.MirrorC")}),-1.0]])]});
            var Q47;
            Q47=makeQuery(id+"F0.imprint","IMPRINT",FACE,{"disambiguationData":[TD([[makeQuery(id+"F0.imprint","IMPRINT",EDGE,{"derivedFrom":sQuery(id+"F0.wireOp",EDGE,"E37.MirrorC")}),-1.0]])]});
            var Q48;
            Q48=makeQuery(id+"F0.imprint","IMPRINT",FACE,{"disambiguationData":[TD([[makeQuery(id+"F0.imprint","IMPRINT",EDGE,{"derivedFrom":sQuery(id+"F0.wireOp",EDGE,"E36.MirrorC")}),-1.0]])]});
            var Q49;
            Q49=makeQuery(id+"F0.imprint","IMPRINT",FACE,{"disambiguationData":[TD([[makeQuery(id+"F0.imprint","IMPRINT",EDGE,{"derivedFrom":sQuery(id+"F0.wireOp",EDGE,"E35.MirrorC")}),-1.0]])]});
            var Q50;
            Q50=makeQuery(id+"F0.imprint","IMPRINT",FACE,{"disambiguationData":[TD([[makeQuery(id+"F0.imprint","IMPRINT",EDGE,{"derivedFrom":sQuery(id+"F0.wireOp",EDGE,"E34.MirrorC")}),-1.0]])]});
            var Q51;
            Q51=makeQuery(id+"F0.imprint","IMPRINT",FACE,{"disambiguationData":[TD([[makeQuery(id+"F0.imprint","IMPRINT",EDGE,{"derivedFrom":sQuery(id+"F0.wireOp",EDGE,"E33.MirrorC")}),-1.0]])]});
            var Q52;
            Q52=makeQuery(id+"F0.imprint","IMPRINT",FACE,{"disambiguationData":[TD([[makeQuery(id+"F0.imprint","IMPRINT",EDGE,{"derivedFrom":sQuery(id+"F0.wireOp",EDGE,"E32.MirrorC")}),-1.0]])]});
            var Q53;
            Q53=makeQuery(id+"F0.imprint","IMPRINT",FACE,{"disambiguationData":[TD([[makeQuery(id+"F0.imprint","IMPRINT",EDGE,{"derivedFrom":sQuery(id+"F0.wireOp",EDGE,"E30")}),1.0]])]});
            var Q54;
            Q54=makeQuery(id+"F0.imprint","IMPRINT",FACE,{"disambiguationData":[TD([[makeQuery(id+"F0.imprint","IMPRINT",EDGE,{"derivedFrom":sQuery(id+"F0.wireOp",EDGE,"E29")}),1.0]])]});
            var Q55;
            Q55=makeQuery(id+"F0.imprint","IMPRINT",FACE,{"disambiguationData":[TD([[makeQuery(id+"F0.imprint","IMPRINT",EDGE,{"derivedFrom":sQuery(id+"F0.wireOp",EDGE,"E28")}),1.0]])]});
            var Q56;
            Q56=makeQuery(id+"F0.imprint","IMPRINT",FACE,{"disambiguationData":[TD([[makeQuery(id+"F0.imprint","IMPRINT",EDGE,{"derivedFrom":sQuery(id+"F0.wireOp",EDGE,"E27")}),1.0]])]});
            var Q57;
            Q57=makeQuery(id+"F0.imprint","IMPRINT",FACE,{"disambiguationData":[TD([[makeQuery(id+"F0.imprint","IMPRINT",EDGE,{"derivedFrom":sQuery(id+"F0.wireOp",EDGE,"E25")}),1.0]])]});
            var Q58;
            Q58=makeQuery(id+"F0.imprint","IMPRINT",FACE,{"disambiguationData":[TD([[makeQuery(id+"F0.imprint","IMPRINT",EDGE,{"derivedFrom":sQuery(id+"F0.wireOp",EDGE,"E26")}),1.0]])]});
            var Q59;
            Q59=makeQuery(id+"F0.imprint","IMPRINT",FACE,{"disambiguationData":[TD([[makeQuery(id+"F0.imprint","IMPRINT",EDGE,{"derivedFrom":sQuery(id+"F0.wireOp",EDGE,"E24")}),1.0]])]});
            var Q60;
            Q60=makeQuery(id+"F0.imprint","IMPRINT",FACE,{"disambiguationData":[TD([[makeQuery(id+"F0.imprint","IMPRINT",EDGE,{"derivedFrom":sQuery(id+"F0.wireOp",EDGE,"E23")}),1.0]])]});
            var Q61;
            Q61=makeQuery(id+"F0.imprint","IMPRINT",FACE,{"disambiguationData":[TD([[makeQuery(id+"F0.imprint","IMPRINT",EDGE,{"derivedFrom":sQuery(id+"F0.wireOp",EDGE,"234bdb74-ce79-4044-9d0f-a6978c3c29130.MirrorC")}),-1.0]])]});
            var Q62;
            Q62=makeQuery(id+"F1.opExtrude","CAP_FACE",FACE,{"disambiguationData":[OSD([sQuery(id+"F0.wireOp",EDGE,"0dDpVTIy-GunA-bBvD-cwDT-sV3W6Ews1qMp"),sQuery(id+"F0.wireOp",EDGE,"DaxXs096-5P6e-ln3i-1fls-EDtKtiFNkicc"),sQuery(id+"F0.wireOp",EDGE,"9CA4RQp1-Vh6f-FTdw-iHL7-ZiKy4ZHbnpA4"),sQuery(id+"F0.wireOp",EDGE,"8MmCyf6s-D1jL-yhrz-7HK1-GQKixaBdKuq5")])],"isStart":false});
            var Q63;
            Q63=makeQuery(id+"F1.opExtrude","CAP_FACE",FACE,{"disambiguationData":[OSD([sQuery(id+"F0.wireOp",EDGE,"0dbe8d11-749e-4dd8-bf5f-606088edf9f927.MirrorC"),sQuery(id+"F0.wireOp",EDGE,"0dbe8d11-749e-4dd8-bf5f-606088edf9f930.MirrorC"),sQuery(id+"F0.wireOp",EDGE,"0dbe8d11-749e-4dd8-bf5f-606088edf9f937.MirrorC"),sQuery(id+"F0.wireOp",EDGE,"0dbe8d11-749e-4dd8-bf5f-606088edf9f939.MirrorC")])],"isStart":false});
            var Q64;
            {var subQ6=sQuery(id+"F0.wireOp",EDGE,"E11");Q64=makeQuery(id+"F0.imprint","IMPRINT",FACE,{"disambiguationData":[TD([[makeQuery(id+"F0.imprint","IMPRINT",EDGE,{"derivedFrom":subQ6}),-1.0]])]});}
            var Q65;
            {var subQ6=sQuery(id+"F0.wireOp",EDGE,"0dbe8d11-749e-4dd8-bf5f-606088edf9f936.MirrorCS");Q65=makeQuery(id+"F0.imprint","IMPRINT",FACE,{"disambiguationData":[TD([[makeQuery(id+"F0.imprint","IMPRINT",EDGE,{"derivedFrom":subQ6}),-1.0]])]});}
            var Q66;
            {var subQ0=sQuery(id+"F0.wireOp",EDGE,"edc6cb30-b65f-47d9-9bdc-20ee79fae63b161.MirrorCS");var subQ1=sQuery(id+"F0.wireOp",EDGE,"edc6cb30-b65f-47d9-9bdc-20ee79fae63b146.MirrorCS");var subQ2=makeQuery(id+"F0.imprint","INTERSECT",VERTEX,{"derivedFrom":[subQ1,subQ0]});Q66=makeQuery(id+"F0.imprint","IMPRINT",FACE,{"disambiguationData":[TD([[makeQuery(id+"F0.imprint","IMPRINT",EDGE,{"disambiguationData":[TD([[subQ2,-1.0]])],"derivedFrom":subQ1}),1.0]])]});}
            var Q67;
            Q67=makeQuery(id+"F0.imprint","IMPRINT",FACE,{"disambiguationData":[TD([[makeQuery(id+"F0.imprint","IMPRINT",EDGE,{"derivedFrom":sQuery(id+"F0.wireOp",EDGE,"edc6cb30-b65f-47d9-9bdc-20ee79fae63b149.MirrorC")}),-1.0]])]});
            var Q68;
            Q68=makeQuery(id+"F0.imprint","IMPRINT",FACE,{"disambiguationData":[TD([[makeQuery(id+"F0.imprint","IMPRINT",EDGE,{"derivedFrom":sQuery(id+"F0.wireOp",EDGE,"edc6cb30-b65f-47d9-9bdc-20ee79fae63b157.MirrorC")}),-1.0]])]});
            var Q69;
            Q69=makeQuery(id+"F0.imprint","IMPRINT",FACE,{"disambiguationData":[TD([[makeQuery(id+"F0.imprint","IMPRINT",EDGE,{"derivedFrom":sQuery(id+"F0.wireOp",EDGE,"edc6cb30-b65f-47d9-9bdc-20ee79fae63b132.MirrorC")}),-1.0]])]});
            var Q70;
            Q70=makeQuery(id+"F0.imprint","IMPRINT",FACE,{"disambiguationData":[TD([[makeQuery(id+"F0.imprint","IMPRINT",EDGE,{"derivedFrom":sQuery(id+"F0.wireOp",EDGE,"edc6cb30-b65f-47d9-9bdc-20ee79fae63b153.MirrorC")}),-1.0]])]});
            var Q71;
            Q71=makeQuery(id+"F0.imprint","IMPRINT",FACE,{"disambiguationData":[TD([[makeQuery(id+"F0.imprint","IMPRINT",EDGE,{"derivedFrom":sQuery(id+"F0.wireOp",EDGE,"edc6cb30-b65f-47d9-9bdc-20ee79fae63b150.MirrorC")}),-1.0]])]});
            var Q72;
            Q72=makeQuery(id+"F0.imprint","IMPRINT",FACE,{"disambiguationData":[TD([[makeQuery(id+"F0.imprint","IMPRINT",EDGE,{"derivedFrom":sQuery(id+"F0.wireOp",EDGE,"edc6cb30-b65f-47d9-9bdc-20ee79fae63b123.MirrorC")}),-1.0]])]});
            var Q73;
            Q73=makeQuery(id+"F0.imprint","IMPRINT",FACE,{"disambiguationData":[TD([[makeQuery(id+"F0.imprint","IMPRINT",EDGE,{"derivedFrom":sQuery(id+"F0.wireOp",EDGE,"edc6cb30-b65f-47d9-9bdc-20ee79fae63b160.MirrorC")}),-1.0]])]});
            var Q74;
            Q74=makeQuery(id+"F0.imprint","IMPRINT",FACE,{"disambiguationData":[TD([[makeQuery(id+"F0.imprint","IMPRINT",EDGE,{"derivedFrom":sQuery(id+"F0.wireOp",EDGE,"edc6cb30-b65f-47d9-9bdc-20ee79fae63b128.MirrorC")}),-1.0]])]});
            var Q75;
            Q75=makeQuery(id+"F0.imprint","IMPRINT",FACE,{"disambiguationData":[TD([[makeQuery(id+"F0.imprint","IMPRINT",EDGE,{"derivedFrom":sQuery(id+"F0.wireOp",EDGE,"edc6cb30-b65f-47d9-9bdc-20ee79fae63b144.MirrorC")}),1.0]])]});
            var Q76;
            Q76=makeQuery(id+"F0.imprint","IMPRINT",FACE,{"disambiguationData":[TD([[makeQuery(id+"F0.imprint","IMPRINT",EDGE,{"derivedFrom":sQuery(id+"F0.wireOp",EDGE,"edc6cb30-b65f-47d9-9bdc-20ee79fae63b133.MirrorC")}),1.0]])]});
            var Q77;
            Q77=makeQuery(id+"F0.imprint","IMPRINT",FACE,{"disambiguationData":[TD([[makeQuery(id+"F0.imprint","IMPRINT",EDGE,{"derivedFrom":sQuery(id+"F0.wireOp",EDGE,"edc6cb30-b65f-47d9-9bdc-20ee79fae63b127.MirrorC")}),1.0]])]});
            var Q78;
            Q78=makeQuery(id+"F0.imprint","IMPRINT",FACE,{"disambiguationData":[TD([[makeQuery(id+"F0.imprint","IMPRINT",EDGE,{"derivedFrom":sQuery(id+"F0.wireOp",EDGE,"edc6cb30-b65f-47d9-9bdc-20ee79fae63b126.MirrorC")}),1.0]])]});
            var Q79;
            Q79=makeQuery(id+"F0.imprint","IMPRINT",FACE,{"disambiguationData":[TD([[makeQuery(id+"F0.imprint","IMPRINT",EDGE,{"derivedFrom":sQuery(id+"F0.wireOp",EDGE,"edc6cb30-b65f-47d9-9bdc-20ee79fae63b143.MirrorC")}),1.0]])]});
            var Q80;
            Q80=makeQuery(id+"F0.imprint","IMPRINT",FACE,{"disambiguationData":[TD([[makeQuery(id+"F0.imprint","IMPRINT",EDGE,{"derivedFrom":sQuery(id+"F0.wireOp",EDGE,"edc6cb30-b65f-47d9-9bdc-20ee79fae63b159.MirrorC")}),1.0]])]});
            var Q81;
            Q81=makeQuery(id+"F0.imprint","IMPRINT",FACE,{"disambiguationData":[TD([[makeQuery(id+"F0.imprint","IMPRINT",EDGE,{"derivedFrom":sQuery(id+"F0.wireOp",EDGE,"edc6cb30-b65f-47d9-9bdc-20ee79fae63b136.MirrorC")}),1.0]])]});
            var Q82;
            Q82=makeQuery(id+"F0.imprint","IMPRINT",FACE,{"disambiguationData":[TD([[makeQuery(id+"F0.imprint","IMPRINT",EDGE,{"derivedFrom":sQuery(id+"F0.wireOp",EDGE,"edc6cb30-b65f-47d9-9bdc-20ee79fae63b164.MirrorC")}),1.0]])]});
            var Q83;
            Q83=makeQuery(id+"F0.imprint","IMPRINT",FACE,{"disambiguationData":[TD([[makeQuery(id+"F0.imprint","IMPRINT",EDGE,{"derivedFrom":sQuery(id+"F0.wireOp",EDGE,"edc6cb30-b65f-47d9-9bdc-20ee79fae63b119.MirrorC")}),-1.0]])]});
            var Q84;
            Q84=makeQuery(id+"F0.imprint","IMPRINT",FACE,{"disambiguationData":[TD([[makeQuery(id+"F0.imprint","IMPRINT",EDGE,{"derivedFrom":sQuery(id+"F0.wireOp",EDGE,"edc6cb30-b65f-47d9-9bdc-20ee79fae63b141.MirrorC")}),-1.0]])]});
            var Q85;
            Q85=makeQuery(id+"F0.imprint","IMPRINT",FACE,{"disambiguationData":[TD([[makeQuery(id+"F0.imprint","IMPRINT",EDGE,{"derivedFrom":sQuery(id+"F0.wireOp",EDGE,"edc6cb30-b65f-47d9-9bdc-20ee79fae63b125.MirrorC")}),1.0]])]});
            var Q86;
            Q86=makeQuery(id+"F0.imprint","IMPRINT",FACE,{"disambiguationData":[TD([[makeQuery(id+"F0.imprint","IMPRINT",EDGE,{"derivedFrom":sQuery(id+"F0.wireOp",EDGE,"edc6cb30-b65f-47d9-9bdc-20ee79fae63b154.MirrorC")}),1.0]])]});
            var Q87;
            Q87=makeQuery(id+"F0.imprint","IMPRINT",FACE,{"disambiguationData":[TD([[makeQuery(id+"F0.imprint","IMPRINT",EDGE,{"derivedFrom":sQuery(id+"F0.wireOp",EDGE,"edc6cb30-b65f-47d9-9bdc-20ee79fae63b145.MirrorC")}),1.0]])]});
            var Q88;
            Q88=makeQuery(id+"F0.imprint","IMPRINT",FACE,{"disambiguationData":[TD([[makeQuery(id+"F0.imprint","IMPRINT",EDGE,{"derivedFrom":sQuery(id+"F0.wireOp",EDGE,"edc6cb30-b65f-47d9-9bdc-20ee79fae63b139.MirrorC")}),1.0]])]});
            var Q89;
            Q89=makeQuery(id+"F0.imprint","IMPRINT",FACE,{"disambiguationData":[TD([[makeQuery(id+"F0.imprint","IMPRINT",EDGE,{"derivedFrom":sQuery(id+"F0.wireOp",EDGE,"edc6cb30-b65f-47d9-9bdc-20ee79fae63b162.MirrorC")}),1.0]])]});
            var Q90;
            Q90=makeQuery(id+"F0.imprint","IMPRINT",FACE,{"disambiguationData":[TD([[makeQuery(id+"F0.imprint","IMPRINT",EDGE,{"derivedFrom":sQuery(id+"F0.wireOp",EDGE,"edc6cb30-b65f-47d9-9bdc-20ee79fae63b140.MirrorC")}),1.0]])]});
            var Q91;
            Q91=makeQuery(id+"F0.imprint","IMPRINT",FACE,{"disambiguationData":[TD([[makeQuery(id+"F0.imprint","IMPRINT",EDGE,{"derivedFrom":sQuery(id+"F0.wireOp",EDGE,"edc6cb30-b65f-47d9-9bdc-20ee79fae63b156.MirrorC")}),1.0]])]});
            var Q92;
            Q92=makeQuery(id+"F0.imprint","IMPRINT",FACE,{"disambiguationData":[TD([[makeQuery(id+"F0.imprint","IMPRINT",EDGE,{"derivedFrom":sQuery(id+"F0.wireOp",EDGE,"4b3109ea-8a59-4b7b-b5cc-42d9bb3fa2250.MirrorC")}),1.0]])]});
            extrude(context, id + "F2", {"entities" : qUnion([Q0, Q1, Q2, Q3, Q4, Q5, Q6, Q7, Q8, Q9, Q10, Q11, Q12, Q13, Q14, Q15, Q16, Q17, Q18, Q19, Q20, Q21, Q22, Q23, Q24, Q25, Q26, Q27, Q28, Q29, Q30, Q31, Q32, Q33, Q34, Q35, Q36, Q37, Q38, Q39, Q40, Q41, Q42, Q43, Q44, Q45, Q46, Q47, Q48, Q49, Q50, Q51, Q52, Q53, Q54, Q55, Q56, Q57, Q58, Q59, Q60, Q61, Q62, Q63, Q64, Q65, Q66, Q67, Q68, Q69, Q70, Q71, Q72, Q73, Q74, Q75, Q76, Q77, Q78, Q79, Q80, Q81, Q82, Q83, Q84, Q85, Q86, Q87, Q88, Q89, Q90, Q91, Q92]), "oppositeDirection" : true, "depth" : 2 * mm, "offsetDistance" : 25 * mm});
        }
        {
            var Q0;
            Q0=makeQuery(id+"F1.opExtrude","SWEPT_BODY",BODY,{"disambiguationData":[OSD([sQuery(id+"F0.wireOp",EDGE,"E5"),sQuery(id+"F0.wireOp",EDGE,"E6"),sQuery(id+"F0.wireOp",EDGE,"E7.filletArc"),sQuery(id+"F0.wireOp",EDGE,"E8.0"),sQuery(id+"F0.wireOp",EDGE,"E8.1"),sQuery(id+"F0.wireOp",EDGE,"E8.2"),sQuery(id+"F0.wireOp",EDGE,"E9"),sQuery(id+"F0.wireOp",EDGE,"E11"),sQuery(id+"F0.wireOp",EDGE,"E18"),sQuery(id+"F0.wireOp",EDGE,"E19.filletArc"),sQuery(id+"F0.wireOp",EDGE,"E21"),sQuery(id+"F0.wireOp",EDGE,"E23"),sQuery(id+"F0.wireOp",EDGE,"E24"),sQuery(id+"F0.wireOp",EDGE,"E25"),sQuery(id+"F0.wireOp",EDGE,"E26"),sQuery(id+"F0.wireOp",EDGE,"E27"),sQuery(id+"F0.wireOp",EDGE,"E28"),sQuery(id+"F0.wireOp",EDGE,"E29"),sQuery(id+"F0.wireOp",EDGE,"E30"),sQuery(id+"F0.wireOp",EDGE,"E32.MirrorC"),sQuery(id+"F0.wireOp",EDGE,"E33.MirrorC"),sQuery(id+"F0.wireOp",EDGE,"E34.MirrorC"),sQuery(id+"F0.wireOp",EDGE,"E35.MirrorC"),sQuery(id+"F0.wireOp",EDGE,"E36.MirrorC"),sQuery(id+"F0.wireOp",EDGE,"E37.MirrorC"),sQuery(id+"F0.wireOp",EDGE,"E38.MirrorC"),sQuery(id+"F0.wireOp",EDGE,"E39.MirrorC"),sQuery(id+"F0.wireOp",EDGE,"E41.MirrorC"),sQuery(id+"F0.wireOp",EDGE,"E42.MirrorC"),sQuery(id+"F0.wireOp",EDGE,"E43.MirrorC"),sQuery(id+"F0.wireOp",EDGE,"E44.MirrorC"),sQuery(id+"F0.wireOp",EDGE,"E45.MirrorC"),sQuery(id+"F0.wireOp",EDGE,"E46.MirrorC"),sQuery(id+"F0.wireOp",EDGE,"E47.MirrorC"),sQuery(id+"F0.wireOp",EDGE,"E48"),sQuery(id+"F0.wireOp",EDGE,"E49"),sQuery(id+"F0.wireOp",EDGE,"E50"),sQuery(id+"F0.wireOp",EDGE,"E51"),sQuery(id+"F0.wireOp",EDGE,"E52"),sQuery(id+"F0.wireOp",EDGE,"E53"),sQuery(id+"F0.wireOp",EDGE,"E54"),sQuery(id+"F0.wireOp",EDGE,"E55"),sQuery(id+"F0.wireOp",EDGE,"E56"),sQuery(id+"F0.wireOp",EDGE,"E57"),sQuery(id+"F0.wireOp",EDGE,"E58"),sQuery(id+"F0.wireOp",EDGE,"E59"),sQuery(id+"F0.wireOp",EDGE,"E60"),sQuery(id+"F0.wireOp",EDGE,"E61"),sQuery(id+"F0.wireOp",EDGE,"E62"),sQuery(id+"F0.wireOp",EDGE,"E63"),sQuery(id+"F0.wireOp",EDGE,"E64"),sQuery(id+"F0.wireOp",EDGE,"E65"),sQuery(id+"F0.wireOp",EDGE,"E66"),sQuery(id+"F0.wireOp",EDGE,"E67.MirrorCS"),sQuery(id+"F0.wireOp",EDGE,"E71.MirrorCS"),sQuery(id+"F0.wireOp",EDGE,"E72.MirrorCS"),sQuery(id+"F0.wireOp",EDGE,"E73.MirrorCS"),sQuery(id+"F0.wireOp",EDGE,"E74.MirrorCS"),sQuery(id+"F0.wireOp",EDGE,"E75.MirrorCS"),sQuery(id+"F0.wireOp",EDGE,"E76.MirrorCS"),sQuery(id+"F0.wireOp",EDGE,"E77.MirrorCS"),sQuery(id+"F0.wireOp",EDGE,"E78.MirrorCS"),sQuery(id+"F0.wireOp",EDGE,"E79.MirrorCS"),sQuery(id+"F0.wireOp",EDGE,"E80.MirrorCS"),sQuery(id+"F0.wireOp",EDGE,"E81.MirrorCS"),sQuery(id+"F0.wireOp",EDGE,"E69.MirrorCS"),sQuery(id+"F0.wireOp",EDGE,"E70.MirrorCS"),sQuery(id+"F0.wireOp",EDGE,"E68.MirrorCS"),sQuery(id+"F0.wireOp",EDGE,"E82.MirrorCS"),sQuery(id+"F0.wireOp",EDGE,"E83"),sQuery(id+"F0.wireOp",EDGE,"E84"),sQuery(id+"F0.wireOp",EDGE,"E85"),sQuery(id+"F0.wireOp",EDGE,"E86"),sQuery(id+"F0.wireOp",EDGE,"E87"),sQuery(id+"F0.wireOp",EDGE,"E88"),sQuery(id+"F0.wireOp",EDGE,"E89"),sQuery(id+"F0.wireOp",EDGE,"E90"),sQuery(id+"F0.wireOp",EDGE,"E91"),sQuery(id+"F0.wireOp",EDGE,"E92"),sQuery(id+"F0.wireOp",EDGE,"E93"),sQuery(id+"F0.wireOp",EDGE,"E94"),sQuery(id+"F0.wireOp",EDGE,"E95"),sQuery(id+"F0.wireOp",EDGE,"E96"),sQuery(id+"F0.wireOp",EDGE,"E97"),sQuery(id+"F0.wireOp",EDGE,"E98"),sQuery(id+"F0.wireOp",EDGE,"E99.MirrorCS"),sQuery(id+"F0.wireOp",EDGE,"E100.MirrorCS"),sQuery(id+"F0.wireOp",EDGE,"E101.MirrorCS"),sQuery(id+"F0.wireOp",EDGE,"E102.MirrorCS"),sQuery(id+"F0.wireOp",EDGE,"E103.MirrorCS"),sQuery(id+"F0.wireOp",EDGE,"E104.MirrorCS"),sQuery(id+"F0.wireOp",EDGE,"E105.MirrorCS"),sQuery(id+"F0.wireOp",EDGE,"E106.MirrorCS"),sQuery(id+"F0.wireOp",EDGE,"E107.MirrorCS"),sQuery(id+"F0.wireOp",EDGE,"E108.MirrorCS"),sQuery(id+"F0.wireOp",EDGE,"E109.MirrorCS"),sQuery(id+"F0.wireOp",EDGE,"E110.MirrorCS"),sQuery(id+"F0.wireOp",EDGE,"E111.MirrorCS"),sQuery(id+"F0.wireOp",EDGE,"E112.MirrorCS"),sQuery(id+"F0.wireOp",EDGE,"E113.MirrorCS"),sQuery(id+"F0.wireOp",EDGE,"E114.MirrorCS"),sQuery(id+"F0.wireOp",EDGE,"E115"),sQuery(id+"F0.wireOp",EDGE,"E116"),sQuery(id+"F0.wireOp",EDGE,"E117"),sQuery(id+"F0.wireOp",EDGE,"E118"),sQuery(id+"F0.wireOp",EDGE,"E119"),sQuery(id+"F0.wireOp",EDGE,"E120"),sQuery(id+"F0.wireOp",EDGE,"E121"),sQuery(id+"F0.wireOp",EDGE,"E122"),sQuery(id+"F0.wireOp",EDGE,"E123"),sQuery(id+"F0.wireOp",EDGE,"E124"),sQuery(id+"F0.wireOp",EDGE,"E125"),sQuery(id+"F0.wireOp",EDGE,"E126"),sQuery(id+"F0.wireOp",EDGE,"E127"),sQuery(id+"F0.wireOp",EDGE,"E128"),sQuery(id+"F0.wireOp",EDGE,"E129"),sQuery(id+"F0.wireOp",EDGE,"E130"),sQuery(id+"F0.wireOp",EDGE,"E131.MirrorCS"),sQuery(id+"F0.wireOp",EDGE,"E132.MirrorCS"),sQuery(id+"F0.wireOp",EDGE,"E133.MirrorCS"),sQuery(id+"F0.wireOp",EDGE,"E134.MirrorCS"),sQuery(id+"F0.wireOp",EDGE,"E135.MirrorCS"),sQuery(id+"F0.wireOp",EDGE,"E136.MirrorCS"),sQuery(id+"F0.wireOp",EDGE,"E137.MirrorCS"),sQuery(id+"F0.wireOp",EDGE,"E138.MirrorCS"),sQuery(id+"F0.wireOp",EDGE,"E139.MirrorCS"),sQuery(id+"F0.wireOp",EDGE,"E140.MirrorCS"),sQuery(id+"F0.wireOp",EDGE,"E141.MirrorCS"),sQuery(id+"F0.wireOp",EDGE,"E142.MirrorCS"),sQuery(id+"F0.wireOp",EDGE,"E143.MirrorCS"),sQuery(id+"F0.wireOp",EDGE,"E144.MirrorCS"),sQuery(id+"F0.wireOp",EDGE,"E145.MirrorCS"),sQuery(id+"F0.wireOp",EDGE,"E146.MirrorCS"),sQuery(id+"F0.wireOp",EDGE,"E147.MirrorCS"),sQuery(id+"F0.wireOp",EDGE,"E148.MirrorCS"),sQuery(id+"F0.wireOp",EDGE,"E149.MirrorCS"),sQuery(id+"F0.wireOp",EDGE,"E150.MirrorCS"),sQuery(id+"F0.wireOp",EDGE,"E151.MirrorCS"),sQuery(id+"F0.wireOp",EDGE,"E152.MirrorCS"),sQuery(id+"F0.wireOp",EDGE,"E153.MirrorCS"),sQuery(id+"F0.wireOp",EDGE,"E154.MirrorCS"),sQuery(id+"F0.wireOp",EDGE,"E155"),sQuery(id+"F0.wireOp",EDGE,"E156"),sQuery(id+"F0.wireOp",EDGE,"E157"),sQuery(id+"F0.wireOp",EDGE,"E158"),sQuery(id+"F0.wireOp",EDGE,"E160")])]});
            var Q1;
            Q1=makeQuery(id+"F2.opExtrude","SWEPT_BODY",BODY,{"disambiguationData":[OSD([sQuery(id+"F0.wireOp",EDGE,"E5"),sQuery(id+"F0.wireOp",EDGE,"E6"),sQuery(id+"F0.wireOp",EDGE,"E7.filletArc"),sQuery(id+"F0.wireOp",EDGE,"E8.0"),sQuery(id+"F0.wireOp",EDGE,"E8.1"),sQuery(id+"F0.wireOp",EDGE,"E8.2"),sQuery(id+"F0.wireOp",EDGE,"E9"),sQuery(id+"F0.wireOp",EDGE,"E13"),sQuery(id+"F0.wireOp",EDGE,"E14"),sQuery(id+"F0.wireOp",EDGE,"E15"),sQuery(id+"F0.wireOp",EDGE,"E16.filletArc"),sQuery(id+"F0.wireOp",EDGE,"E17"),sQuery(id+"F0.wireOp",EDGE,"E18"),sQuery(id+"F0.wireOp",EDGE,"E19.filletArc"),sQuery(id+"F0.wireOp",EDGE,"E21"),sQuery(id+"F0.wireOp",EDGE,"E160")])]});
            var Q2;
            Q2=makeQuery(id+"F1.opExtrude","SWEPT_BODY",BODY,{"disambiguationData":[OSD([sQuery(id+"F0.wireOp",EDGE,"E14"),sQuery(id+"F0.wireOp",EDGE,"E17")])]});
            var Q3;
            Q3=qCreatedBy(makeId("Right.planeOp"),FACE);
            mirror(context, id + "F3", {"entities" : qUnion([Q0, Q1, Q2]), "mirrorPlane" : qUnion([Q3])});
        }
    });
